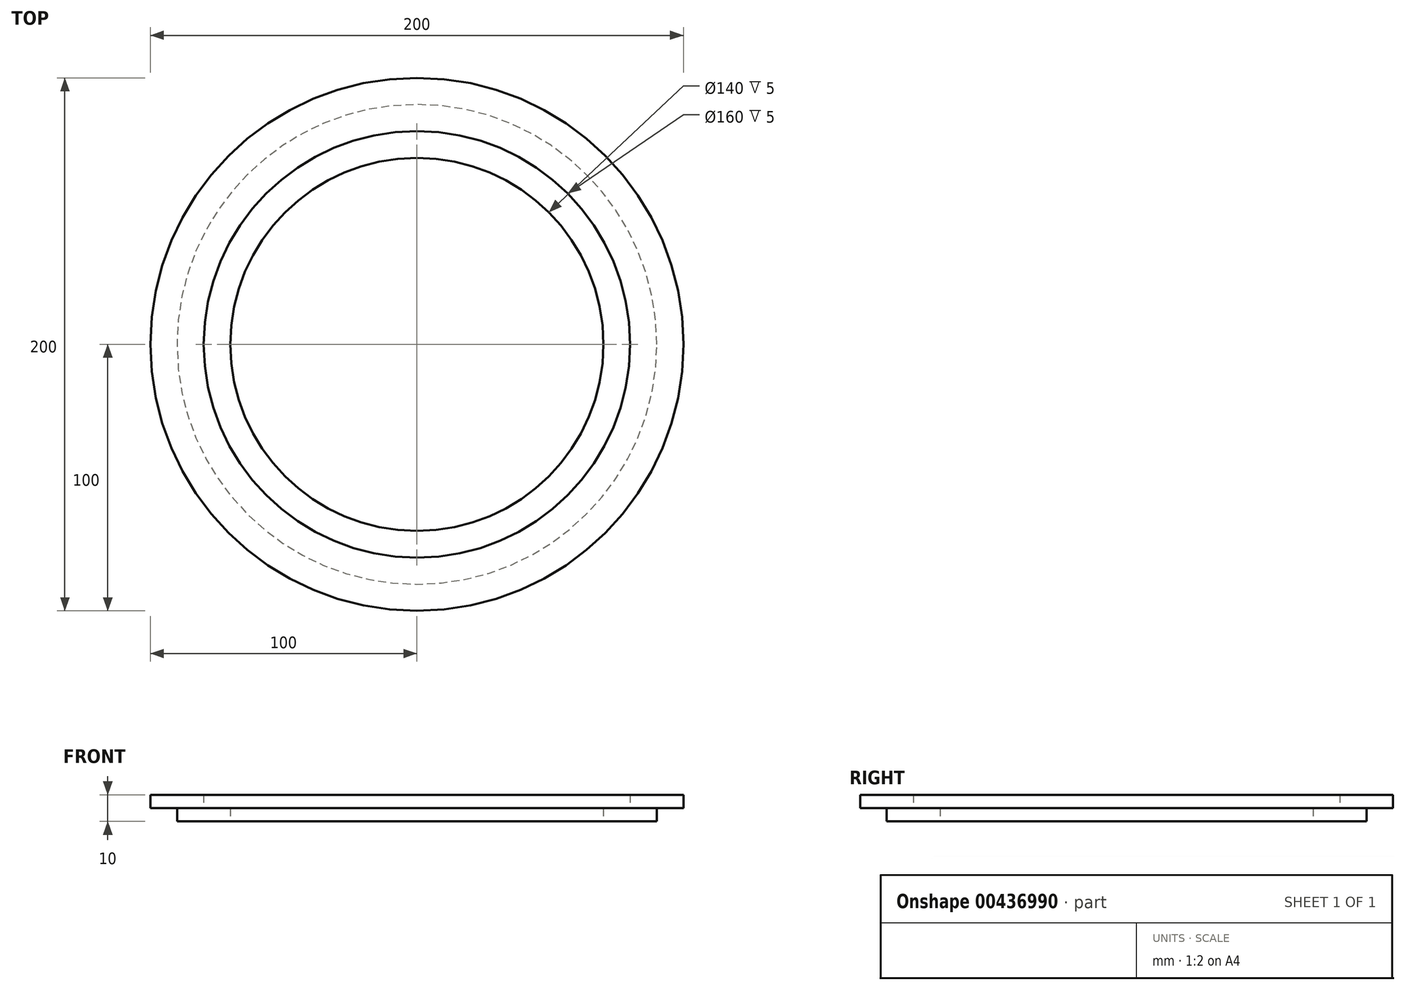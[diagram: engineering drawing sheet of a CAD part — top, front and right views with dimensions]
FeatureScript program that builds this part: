
annotation { "Feature Type Name" : "Feature", "Feature Type Description" : "" }
export const myFeature = defineFeature(function(context is Context, id is Id, definition is map)
    precondition{}
    {
        {
            var Q0;
            Q0=qCreatedBy(makeId("Front.planeOp"),FACE);
            var sketch = newSketch(context, id + "F0", { "sketchPlane" : qUnion([Q0])});
            skLineSegment(sketch, "E0", {"start": v(70, 0) * mm, "end": v(90, 0) * mm});
            skLineSegment(sketch, "E1", {"start": v(90, 0) * mm, "end": v(90, 5) * mm});
            skLineSegment(sketch, "E2", {"start": v(90, 5) * mm, "end": v(100, 5) * mm});
            skLineSegment(sketch, "E3", {"start": v(100, 5) * mm, "end": v(100, 10) * mm});
            skLineSegment(sketch, "E4", {"start": v(100, 10) * mm, "end": v(80, 10) * mm});
            skLineSegment(sketch, "E5", {"start": v(80, 10) * mm, "end": v(80, 5) * mm});
            skLineSegment(sketch, "E6", {"start": v(80, 5) * mm, "end": v(70, 5) * mm});
            skLineSegment(sketch, "E7", {"start": v(70, 5) * mm, "end": v(70, 0) * mm});
            skLineSegment(sketch, "E8", {"start": v(0, 0) * mm, "end": v(0, 62.26) * mm, "construction": true});
            skSolve(sketch);
        }
        {
            var Q0;
            Q0=makeQuery(id+"F0.imprint","IMPRINT",FACE,{"disambiguationData":[TD([[makeQuery(id+"F0.imprint","IMPRINT",EDGE,{"derivedFrom":sQuery(id+"F0.wireOp",EDGE,"E0")}),1.0]])]});
            var Q1;
            Q1=sQuery(id+"F0.wireOp",EDGE,"E8");
            revolve(context, id + "F1", {"entities" : qUnion([Q0]), "axis" : qUnion([Q1]), "revolveType" : RevolveType.FULL});
        }
    });
